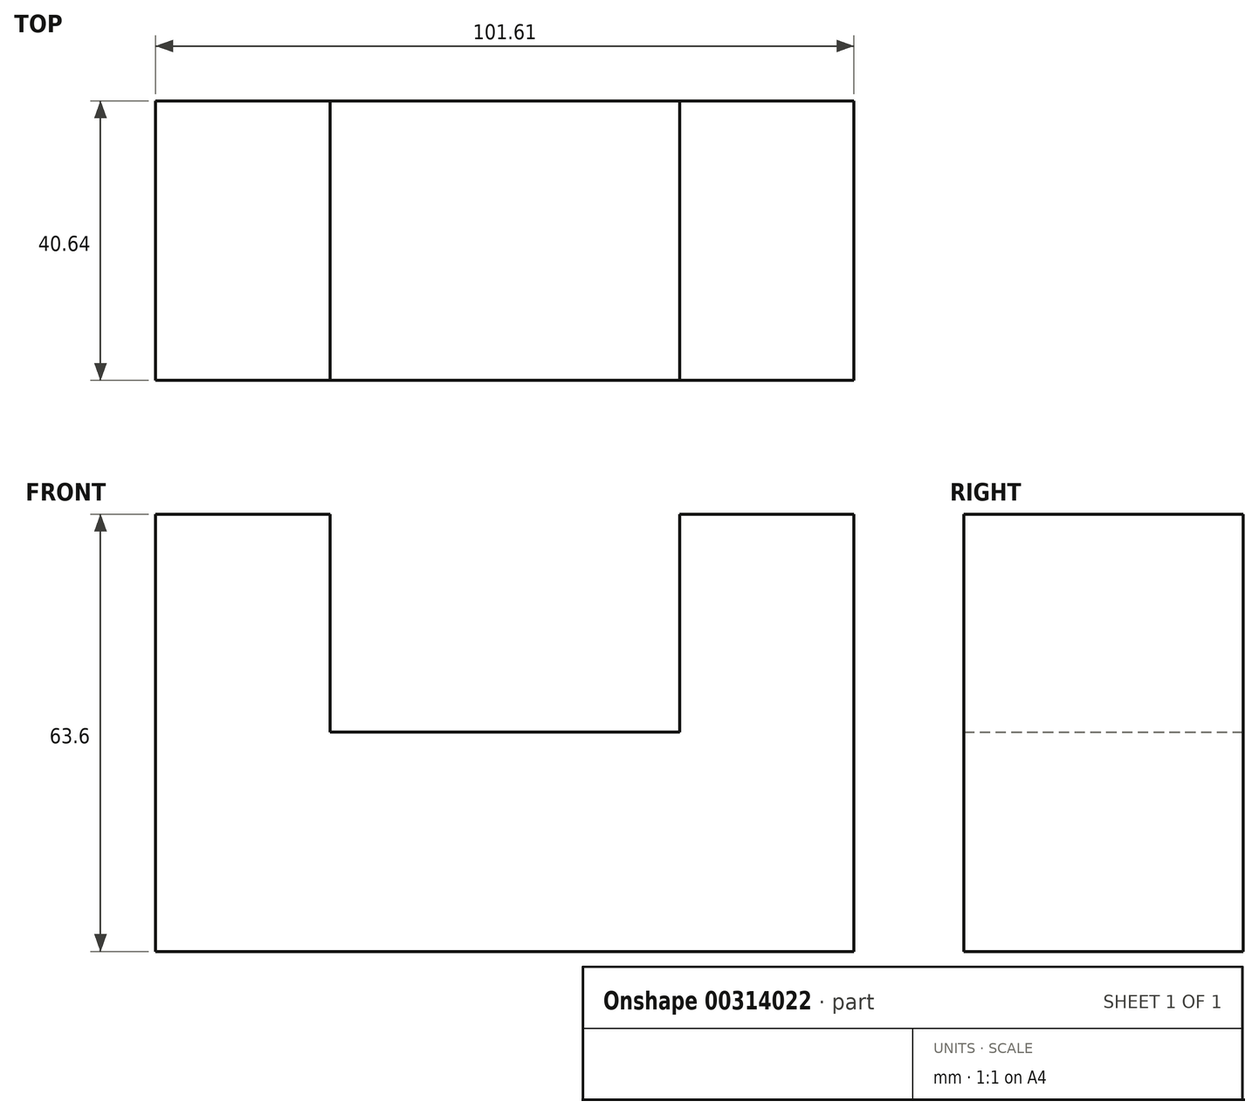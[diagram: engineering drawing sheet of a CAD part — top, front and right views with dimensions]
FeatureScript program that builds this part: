
annotation { "Feature Type Name" : "Feature", "Feature Type Description" : "" }
export const myFeature = defineFeature(function(context is Context, id is Id, definition is map)
    precondition{}
    {
        {
            var Q0;
            Q0=qCreatedBy(makeId("Front.planeOp"),FACE);
            var sketch = newSketch(context, id + "F0", { "sketchPlane" : qUnion([Q0])});
            skLineSegment(sketch, "E0", {"start": v(-60.08, -19.38) * mm, "end": v(41.53, -19.38) * mm});
            skLineSegment(sketch, "E1", {"start": v(41.53, -19.38) * mm, "end": v(41.53, 44.22) * mm});
            skLineSegment(sketch, "E2", {"start": v(41.53, 44.22) * mm, "end": v(16.17, 44.22) * mm});
            skLineSegment(sketch, "E3", {"start": v(-60.08, -19.38) * mm, "end": v(-60.08, 44.22) * mm});
            skLineSegment(sketch, "E4", {"start": v(-60.08, 44.22) * mm, "end": v(-34.67, 44.22) * mm});
            skLineSegment(sketch, "E5", {"start": v(-34.67, 44.22) * mm, "end": v(-34.67, 12.52) * mm});
            skLineSegment(sketch, "E6", {"start": v(16.17, 44.22) * mm, "end": v(16.17, 12.52) * mm});
            skLineSegment(sketch, "E7", {"start": v(16.17, 12.52) * mm, "end": v(-34.67, 12.52) * mm});
            skSolve(sketch);
        }
        {
            var Q0;
            Q0 = qSketchRegion(id + "F0", true);
            extrude(context, id + "F1", {"entities" : qUnion([Q0]), "depth" : 40.64 * mm});
        }
    });
